# Revit family: Leitungsmaterial_Rundleiter_Aluminium
name_source: partatom
category: Generic Models
revit_build: Autodesk Revit 2015 (Build: 20140606_1530(x64)
units: mm (PartAtom-declared; Revit-internal decimal feet)

## types (4) — shared parameters
Manufacturer = OBO Bettermann
Material = Aluminum 6061
URL = http://www.obo-bettermann.com

## per-type parameters (varying)
| type | Diameter dimesion | GTIN | Manufacturer Art. No. |
| RD 8-ALU | 8 mm  [stored 0.0262467 ft] | 4012195381914 | 5021286 |
| RD 8-ALU-T | 8 mm  [stored 0.0262467 ft] | 4012195901273 | 5021294 |
| RD 8-ALU-T 75 | 8 mm  [stored 0.0262467 ft] | 4012196286232 | 5021296 |
| RD 10-ALU | 10 mm  [stored 0.0328084 ft] | 4012195381976 | 5021308 |

note: column(s) folded — value = type name in every type: Article Type

note: [stored X ft] marks values corroborated as IEEE doubles in the binary element streams (Revit-internal decimal feet)

## geometry (parser evidence)
native form markers: Sweep x2
no freeform markers — native parametric forms only
